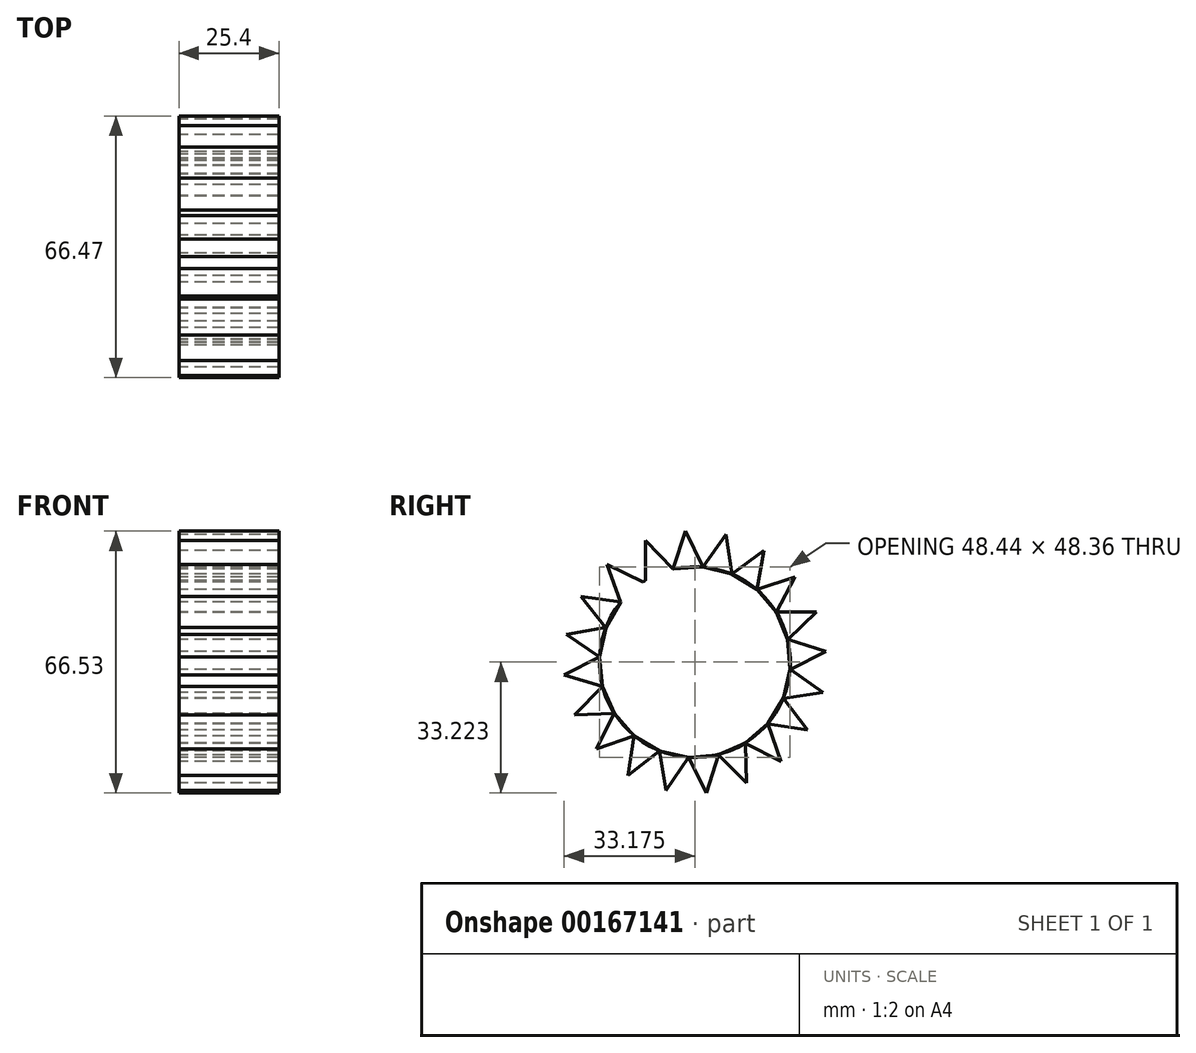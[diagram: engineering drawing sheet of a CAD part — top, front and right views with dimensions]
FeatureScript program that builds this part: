
annotation { "Feature Type Name" : "Feature", "Feature Type Description" : "" }
export const myFeature = defineFeature(function(context is Context, id is Id, definition is map)
    precondition{}
    {
        {
            var Q0;
            Q0=qCreatedBy(makeId("Right.planeOp"),FACE);
            var sketch = newSketch(context, id + "F0", { "sketchPlane" : qUnion([Q0])});
            skCircle(sketch, "E0", {"center": v(0, 0) * mm, "radius": 24.26 * mm});
            skLineSegment(sketch, "E1", {"start": v(-12.52, 20.78) * mm, "end": v(-12.52, 30.94) * mm});
            skLineSegment(sketch, "E2", {"start": v(-12.52, 30.94) * mm, "end": v(-5.45, 23.64) * mm});
            skLineSegment(sketch, "E3", {"start": v(-5.45, 23.64) * mm, "end": v(-12.52, 20.78) * mm});
            skLineSegment(sketch, "E4.1.0", {"start": v(-2.4, 33.29) * mm, "end": v(2.07, 24.17) * mm});
            skLineSegment(sketch, "E4.1.1", {"start": v(2.07, 24.17) * mm, "end": v(-5.53, 23.62) * mm});
            skLineSegment(sketch, "E4.1.2", {"start": v(-5.53, 23.62) * mm, "end": v(-2.4, 33.29) * mm});
            skLineSegment(sketch, "E4.2.0", {"start": v(7.94, 32.42) * mm, "end": v(9.4, 22.36) * mm});
            skLineSegment(sketch, "E4.2.1", {"start": v(9.4, 22.36) * mm, "end": v(2, 24.17) * mm});
            skLineSegment(sketch, "E4.2.2", {"start": v(2, 24.17) * mm, "end": v(7.94, 32.42) * mm});
            skLineSegment(sketch, "E4.3.0", {"start": v(17.52, 28.4) * mm, "end": v(15.82, 18.4) * mm});
            skLineSegment(sketch, "E4.3.1", {"start": v(15.82, 18.4) * mm, "end": v(9.33, 22.4) * mm});
            skLineSegment(sketch, "E4.3.2", {"start": v(9.33, 22.4) * mm, "end": v(17.52, 28.4) * mm});
            skLineSegment(sketch, "E4.4.0", {"start": v(25.4, 21.65) * mm, "end": v(20.7, 12.64) * mm});
            skLineSegment(sketch, "E4.4.1", {"start": v(20.7, 12.64) * mm, "end": v(15.76, 18.44) * mm});
            skLineSegment(sketch, "E4.4.2", {"start": v(15.76, 18.44) * mm, "end": v(25.4, 21.65) * mm});
            skLineSegment(sketch, "E4.5.0", {"start": v(30.82, 12.8) * mm, "end": v(23.59, 5.67) * mm});
            skLineSegment(sketch, "E4.5.1", {"start": v(23.59, 5.67) * mm, "end": v(20.66, 12.7) * mm});
            skLineSegment(sketch, "E4.5.2", {"start": v(20.66, 12.7) * mm, "end": v(30.82, 12.8) * mm});
            skLineSegment(sketch, "E4.6.0", {"start": v(33.26, 2.7) * mm, "end": v(24.19, -1.85) * mm});
            skLineSegment(sketch, "E4.6.1", {"start": v(24.19, -1.85) * mm, "end": v(23.57, 5.74) * mm});
            skLineSegment(sketch, "E4.6.2", {"start": v(23.57, 5.74) * mm, "end": v(33.26, 2.7) * mm});
            skLineSegment(sketch, "E4.7.0", {"start": v(32.49, -7.64) * mm, "end": v(22.45, -9.2) * mm});
            skLineSegment(sketch, "E4.7.1", {"start": v(22.45, -9.2) * mm, "end": v(24.2, -1.78) * mm});
            skLineSegment(sketch, "E4.7.2", {"start": v(24.2, -1.78) * mm, "end": v(32.49, -7.64) * mm});
            skLineSegment(sketch, "E4.8.0", {"start": v(28.57, -17.26) * mm, "end": v(18.54, -15.65) * mm});
            skLineSegment(sketch, "E4.8.1", {"start": v(18.54, -15.65) * mm, "end": v(22.48, -9.12) * mm});
            skLineSegment(sketch, "E4.8.2", {"start": v(22.48, -9.12) * mm, "end": v(28.57, -17.26) * mm});
            skLineSegment(sketch, "E4.9.0", {"start": v(21.88, -25.2) * mm, "end": v(12.83, -20.59) * mm});
            skLineSegment(sketch, "E4.9.1", {"start": v(12.83, -20.59) * mm, "end": v(18.58, -15.59) * mm});
            skLineSegment(sketch, "E4.9.2", {"start": v(18.58, -15.59) * mm, "end": v(21.88, -25.2) * mm});
            skLineSegment(sketch, "E4.10.0", {"start": v(13.08, -30.7) * mm, "end": v(5.88, -23.53) * mm});
            skLineSegment(sketch, "E4.10.1", {"start": v(5.88, -23.53) * mm, "end": v(12.9, -20.55) * mm});
            skLineSegment(sketch, "E4.10.2", {"start": v(12.9, -20.55) * mm, "end": v(13.08, -30.7) * mm});
            skLineSegment(sketch, "E4.11.0", {"start": v(3.01, -33.24) * mm, "end": v(-1.63, -24.2) * mm});
            skLineSegment(sketch, "E4.11.1", {"start": v(-1.63, -24.2) * mm, "end": v(5.96, -23.51) * mm});
            skLineSegment(sketch, "E4.11.2", {"start": v(5.96, -23.51) * mm, "end": v(3.01, -33.24) * mm});
            skLineSegment(sketch, "E4.12.0", {"start": v(-7.34, -32.56) * mm, "end": v(-8.99, -22.53) * mm});
            skLineSegment(sketch, "E4.12.1", {"start": v(-8.99, -22.53) * mm, "end": v(-1.56, -24.2) * mm});
            skLineSegment(sketch, "E4.12.2", {"start": v(-1.56, -24.2) * mm, "end": v(-7.34, -32.56) * mm});
            skLineSegment(sketch, "E4.13.0", {"start": v(-17, -28.72) * mm, "end": v(-15.48, -18.68) * mm});
            skLineSegment(sketch, "E4.13.1", {"start": v(-15.48, -18.68) * mm, "end": v(-8.92, -22.56) * mm});
            skLineSegment(sketch, "E4.13.2", {"start": v(-8.92, -22.56) * mm, "end": v(-17, -28.72) * mm});
            skLineSegment(sketch, "E4.14.0", {"start": v(-25, -22.11) * mm, "end": v(-20.47, -13.02) * mm});
            skLineSegment(sketch, "E4.14.1", {"start": v(-20.47, -13.02) * mm, "end": v(-15.42, -18.73) * mm});
            skLineSegment(sketch, "E4.14.2", {"start": v(-15.42, -18.73) * mm, "end": v(-25, -22.11) * mm});
            skLineSegment(sketch, "E4.15.0", {"start": v(-30.58, -13.36) * mm, "end": v(-23.48, -6.1) * mm});
            skLineSegment(sketch, "E4.15.1", {"start": v(-23.48, -6.1) * mm, "end": v(-20.43, -13.08) * mm});
            skLineSegment(sketch, "E4.15.2", {"start": v(-20.43, -13.08) * mm, "end": v(-30.58, -13.36) * mm});
            skLineSegment(sketch, "E4.16.0", {"start": v(-33.2, -3.32) * mm, "end": v(-24.22, 1.4) * mm});
            skLineSegment(sketch, "E4.16.1", {"start": v(-24.22, 1.4) * mm, "end": v(-23.46, -6.17) * mm});
            skLineSegment(sketch, "E4.16.2", {"start": v(-23.46, -6.17) * mm, "end": v(-33.2, -3.32) * mm});
            skLineSegment(sketch, "E4.17.0", {"start": v(-32.62, 7.05) * mm, "end": v(-22.61, 8.78) * mm});
            skLineSegment(sketch, "E4.17.1", {"start": v(-22.61, 8.78) * mm, "end": v(-24.22, 1.33) * mm});
            skLineSegment(sketch, "E4.17.2", {"start": v(-24.22, 1.33) * mm, "end": v(-32.62, 7.05) * mm});
            skLineSegment(sketch, "E4.18.0", {"start": v(-28.88, 16.73) * mm, "end": v(-18.82, 15.3) * mm});
            skLineSegment(sketch, "E4.18.1", {"start": v(-18.82, 15.3) * mm, "end": v(-22.64, 8.71) * mm});
            skLineSegment(sketch, "E4.18.2", {"start": v(-22.64, 8.71) * mm, "end": v(-28.88, 16.73) * mm});
            skLineSegment(sketch, "E4.19.0", {"start": v(-22.34, 24.8) * mm, "end": v(-13.2, 20.35) * mm});
            skLineSegment(sketch, "E4.19.1", {"start": v(-13.2, 20.35) * mm, "end": v(-18.87, 15.25) * mm});
            skLineSegment(sketch, "E4.19.2", {"start": v(-18.87, 15.25) * mm, "end": v(-22.34, 24.8) * mm});
            skLineSegment(sketch, "E4.anchor1", {"start": v(0, 0) * mm, "end": v(-12.52, 20.78) * mm, "construction": true});
            skLineSegment(sketch, "E4.anchor2", {"start": v(0, 0) * mm, "end": v(-18.87, 15.25) * mm, "construction": true});
            skSolve(sketch);
        }
        {
            var Q0;
            Q0 = qSketchRegion(id + "F0", true);
            extrude(context, id + "F1", {"entities" : qUnion([Q0]), "endBound" : BoundingType.SYMMETRIC, "depth" : 25.4 * mm});
        }
    });
